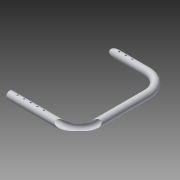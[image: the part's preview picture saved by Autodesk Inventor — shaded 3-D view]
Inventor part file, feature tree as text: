
AUTODESK INVENTOR PART (.ipt)
format: ipt  version: 2015 (Build 190159000, 159)  size: 276,992 bytes
history: native  units: mm
features: other x7, sketch x3, reference x2, sweep x1, hole x1, projected_geometry x1
ambient origin geometry x8: Origin, YZ Plane, XZ Plane, XY Plane, X Axis, Y Axis, Z Axis, Center Point
bodies: Body1 (feature_tree)
feature tree (15):
  other  "Bryła1"
  other  "Płaszczyzna konstrukcyjna1"
  sketch  "Szkic1"
  other  "Płaszczyzna konstrukcyjna2"
  sweep  "Przeciągnięcie1"
  other  "Płaszczyzna konstrukcyjna3"
  hole  "Otwór1"  [1 undecoded]
  other  "Płaszczyzna konstrukcyjna4"
  other  "Płaszczyzna konstrukcyjna5"
  reference  "Odniesienie1"
  sketch  "Szkic2"
  reference  "Odniesienie2"
  sketch  "Szkic3"
  projected_geometry  "Pętla rzutowana1"
  other  "Rzutuj krawędzie tnące1"
note: 1 required parameter value undecoded (feature->parameter linkage not recoverable at this tier; creation-order binding heuristic only, values carry confidence <= 0.55)
